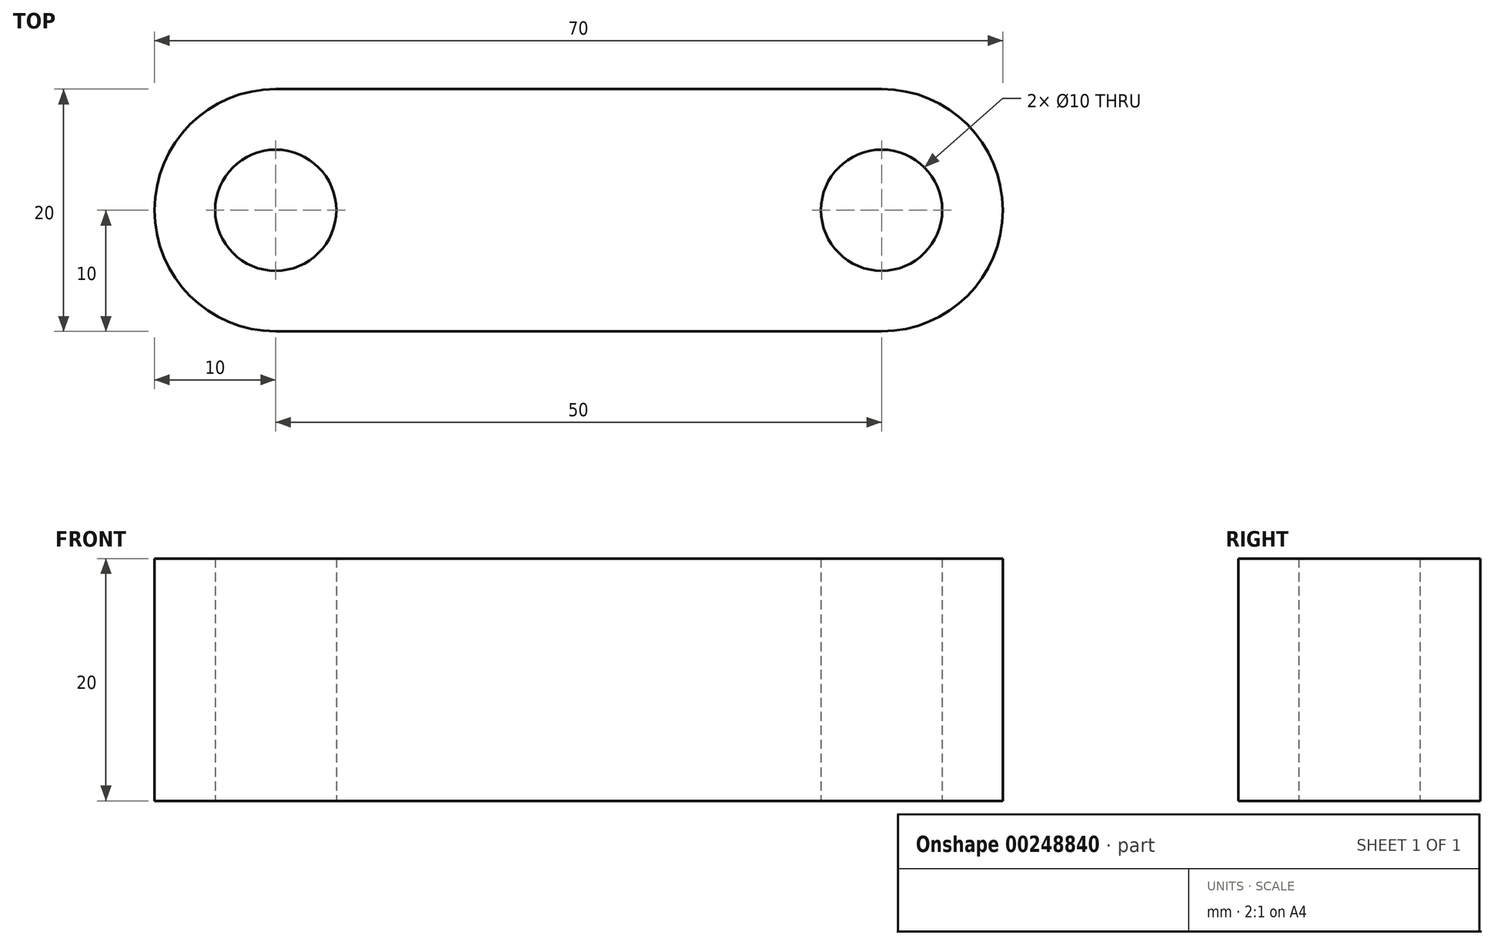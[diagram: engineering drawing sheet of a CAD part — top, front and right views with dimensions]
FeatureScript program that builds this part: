
annotation { "Feature Type Name" : "Feature", "Feature Type Description" : "" }
export const myFeature = defineFeature(function(context is Context, id is Id, definition is map)
    precondition{}
    {
        {
            var Q0;
            Q0=qCreatedBy(makeId("Top.planeOp"),FACE);
            var sketch = newSketch(context, id + "F0", { "sketchPlane" : qUnion([Q0])});
            skLineSegment(sketch, "E0.bottom", {"start": v(25, 10) * mm, "end": v(-25, 10) * mm});
            skLineSegment(sketch, "E0.top", {"start": v(25, -10) * mm, "end": v(-25, -10) * mm});
            skPoint(sketch, "E0.middle", {"position": v(0, 0) * mm});
            skCircle(sketch, "E1", {"center": v(-25, 0) * mm, "radius": 5 * mm});
            skCircle(sketch, "E2", {"center": v(25, 0) * mm, "radius": 5 * mm});
            skArc(sketch, "E3", {"start": v(-25, 10) * mm, "mid": v(-35, 0) * mm, "end": v(-25, -10) * mm});
            skArc(sketch, "E4", {"start": v(25, 10) * mm, "mid": v(35, 0) * mm, "end": v(25, -10) * mm});
            skLineSegment(sketch, "E5", {"start": v(-25, -10) * mm, "end": v(25, -10) * mm});
            skSolve(sketch);
        }
        {
            var Q0;
            Q0=makeQuery(id+"F0.imprint","IMPRINT",FACE,{"disambiguationData":[TD([[makeQuery(id+"F0.imprint","IMPRINT",EDGE,{"derivedFrom":sQuery(id+"F0.wireOp",EDGE,"E0.bottom")}),1.0]])]});
            extrude(context, id + "F1", {"entities" : qUnion([Q0]), "endBound" : BoundingType.SYMMETRIC, "depth" : 20 * mm});
        }
    });
